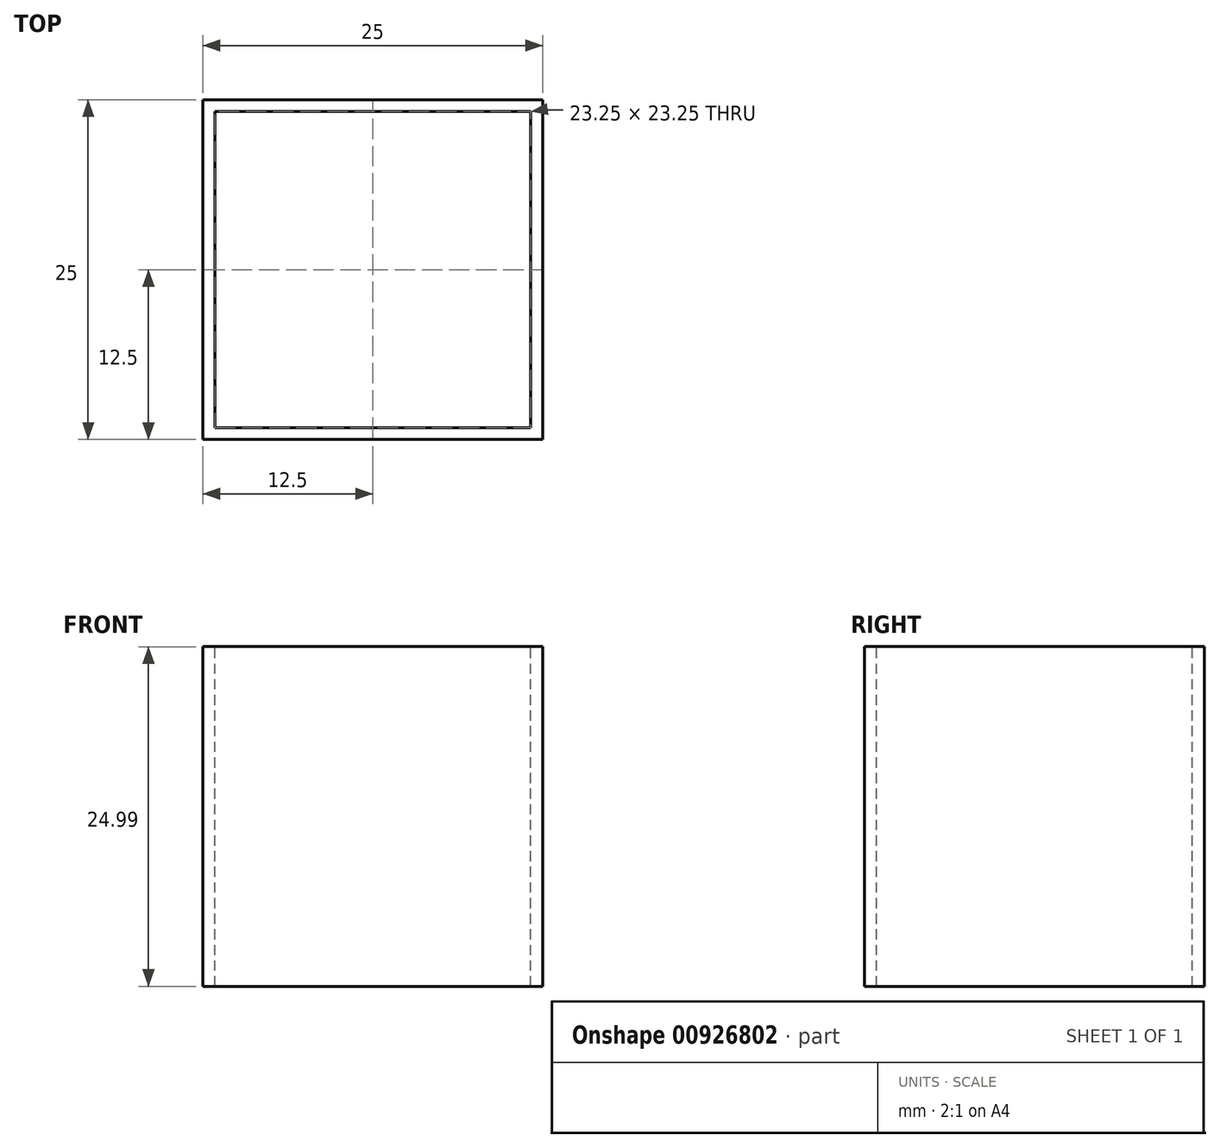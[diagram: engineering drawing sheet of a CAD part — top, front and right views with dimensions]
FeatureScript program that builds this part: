
annotation { "Feature Type Name" : "Feature", "Feature Type Description" : "" }
export const myFeature = defineFeature(function(context is Context, id is Id, definition is map)
    precondition{}
    {
        {
            var Q0;
            Q0=qCreatedBy(makeId("Top.planeOp"),FACE);
            var sketch = newSketch(context, id + "F0", { "sketchPlane" : qUnion([Q0])});
            skLineSegment(sketch, "E0.bottom", {"start": v(12.5, 12.5) * mm, "end": v(-12.5, 12.5) * mm});
            skLineSegment(sketch, "E0.top", {"start": v(12.5, -12.5) * mm, "end": v(-12.5, -12.5) * mm});
            skLineSegment(sketch, "E0.left", {"start": v(12.5, 12.5) * mm, "end": v(12.5, -12.5) * mm});
            skLineSegment(sketch, "E0.right", {"start": v(-12.5, 12.5) * mm, "end": v(-12.5, -12.5) * mm});
            skPoint(sketch, "E0.middle", {"position": v(0, 0) * mm});
            skSolve(sketch);
        }
        {
            var Q0;
            Q0=makeQuery(id+"F0.imprint","IMPRINT",FACE,{"disambiguationData":[TD([[makeQuery(id+"F0.imprint","IMPRINT",EDGE,{"derivedFrom":sQuery(id+"F0.wireOp",EDGE,"E0.bottom")}),1.0]])]});
            extrude(context, id + "F1", {"entities" : qUnion([Q0]), "depth" : 25 * mm, "offsetDistance" : 25.4 * mm});
        }
        {
            var Q0;
            Q0=makeQuery(id+"F1.opExtrude","CAP_FACE",FACE,{"disambiguationData":[OSD([sQuery(id+"F0.wireOp",EDGE,"E0.bottom"),sQuery(id+"F0.wireOp",EDGE,"E0.top"),sQuery(id+"F0.wireOp",EDGE,"E0.left"),sQuery(id+"F0.wireOp",EDGE,"E0.right")])],"isStart":false});
            var sketch = newSketch(context, id + "F2", { "sketchPlane" : qUnion([Q0])});
            skLineSegment(sketch, "E1.bottom", {"start": v(295.27, 334.34) * mm, "end": v(-295.27, 334.34) * mm});
            skLineSegment(sketch, "E1.top", {"start": v(295.27, -334.34) * mm, "end": v(-295.27, -334.34) * mm});
            skLineSegment(sketch, "E1.left", {"start": v(295.28, 334.34) * mm, "end": v(295.28, -334.34) * mm});
            skLineSegment(sketch, "E1.right", {"start": v(-295.28, 334.34) * mm, "end": v(-295.28, -334.34) * mm});
            skPoint(sketch, "E1.middle", {"position": v(0, 0) * mm});
            skLineSegment(sketch, "E2.bottom", {"start": v(11.63, 11.62) * mm, "end": v(-11.62, 11.62) * mm});
            skLineSegment(sketch, "E2.top", {"start": v(11.62, -11.62) * mm, "end": v(-11.63, -11.62) * mm});
            skLineSegment(sketch, "E2.left", {"start": v(11.63, 11.62) * mm, "end": v(11.62, -11.62) * mm});
            skLineSegment(sketch, "E2.right", {"start": v(-11.62, 11.62) * mm, "end": v(-11.63, -11.62) * mm});
            skSolve(sketch);
        }
        {
            var Q0;
            Q0=makeQuery(id+"F2.imprint","IMPRINT",FACE,{"disambiguationData":[TD([[makeQuery(id+"F2.imprint","IMPRINT",EDGE,{"derivedFrom":sQuery(id+"F2.wireOp",EDGE,"E2.bottom")}),1.0]])]});
            extrude(context, id + "F3", {"entities" : qUnion([Q0]), "operationType" : NewBodyOperationType.REMOVE, "depth" : -25 * mm, "offsetDistance" : 25.4 * mm});
        }
    });
